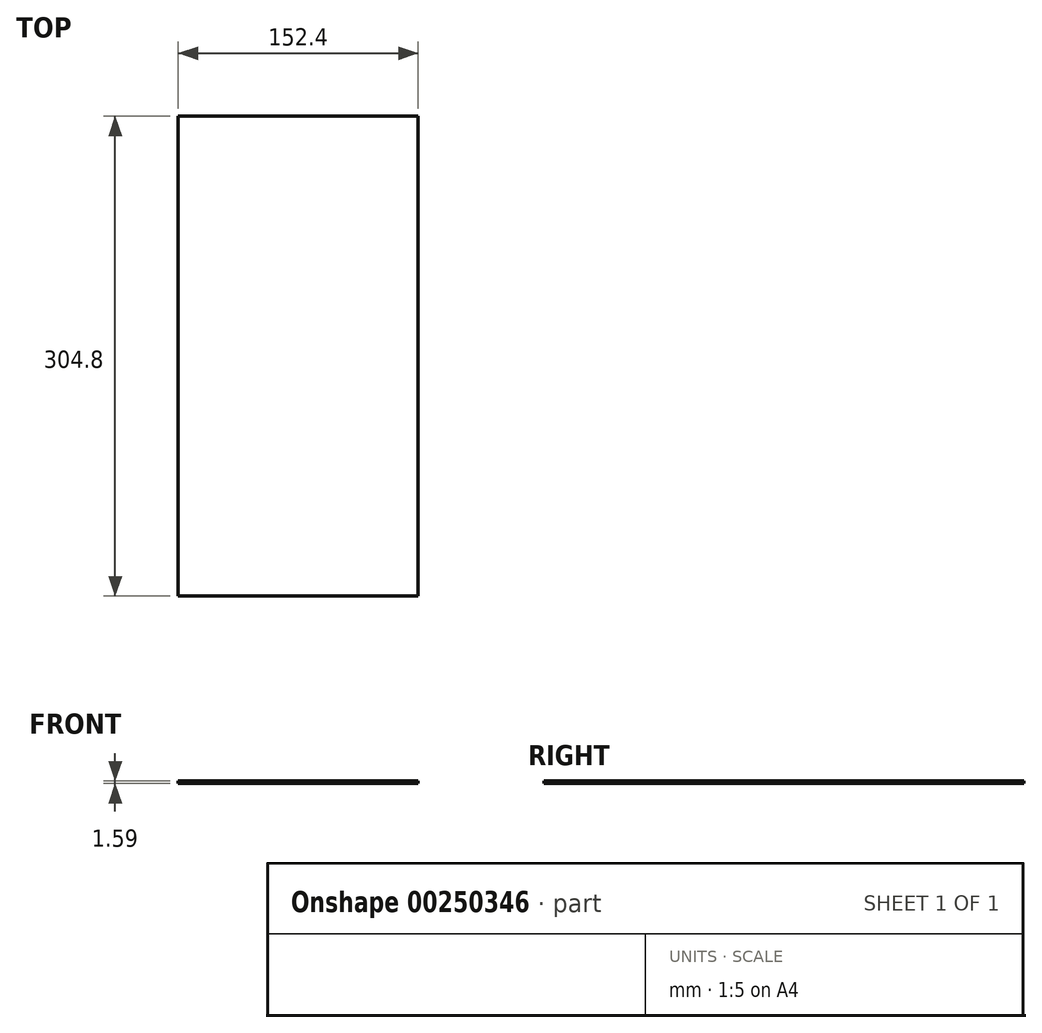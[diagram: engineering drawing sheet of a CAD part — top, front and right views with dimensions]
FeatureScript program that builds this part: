
annotation { "Feature Type Name" : "Feature", "Feature Type Description" : "" }
export const myFeature = defineFeature(function(context is Context, id is Id, definition is map)
    precondition{}
    {
        {
            var Q0;
            Q0=qCreatedBy(makeId("Top.planeOp"),FACE);
            var sketch = newSketch(context, id + "F0", { "sketchPlane" : qUnion([Q0])});
            skLineSegment(sketch, "E0.bottom", {"start": v(76.2, 152.4) * mm, "end": v(-76.2, 152.4) * mm});
            skLineSegment(sketch, "E0.top", {"start": v(76.2, -152.4) * mm, "end": v(-76.2, -152.4) * mm});
            skLineSegment(sketch, "E0.left", {"start": v(76.2, 152.4) * mm, "end": v(76.2, -152.4) * mm});
            skLineSegment(sketch, "E0.right", {"start": v(-76.2, 152.4) * mm, "end": v(-76.2, -152.4) * mm});
            skPoint(sketch, "E0.middle", {"position": v(0, 0) * mm});
            skSolve(sketch);
        }
        {
            var Q0;
            Q0=makeQuery(id+"F0.imprint","IMPRINT",FACE,{"disambiguationData":[TD([[makeQuery(id+"F0.imprint","IMPRINT",EDGE,{"derivedFrom":sQuery(id+"F0.wireOp",EDGE,"E0.bottom")}),1.0]])]});
            extrude(context, id + "F1", {"entities" : qUnion([Q0]), "depth" : 1.59 * mm});
        }
    });
